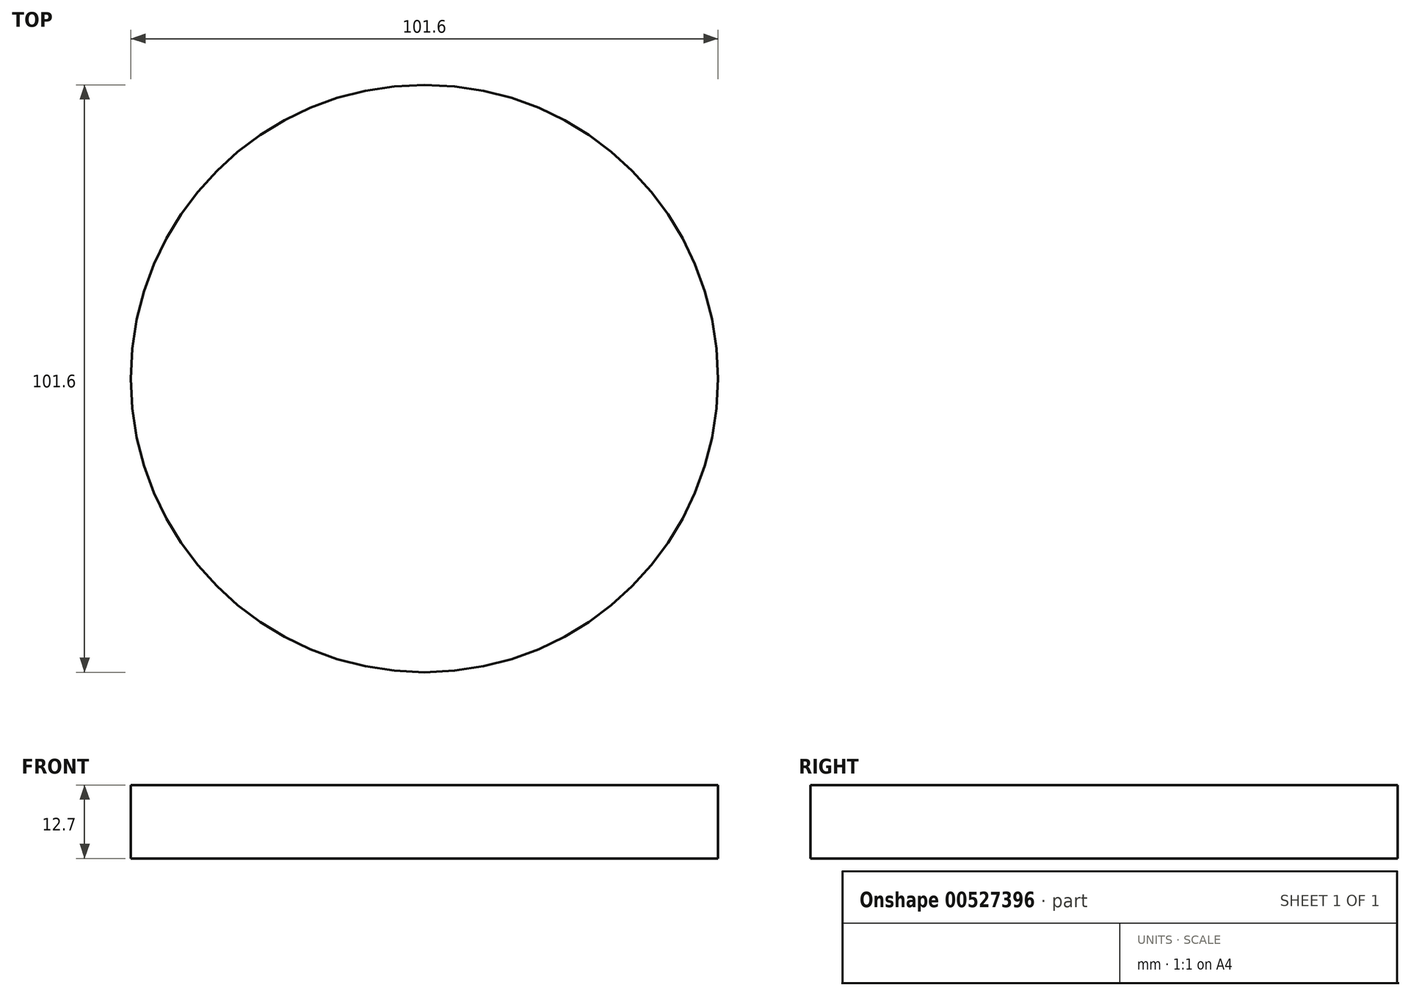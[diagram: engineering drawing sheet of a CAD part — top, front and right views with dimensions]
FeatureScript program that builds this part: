
annotation { "Feature Type Name" : "Feature", "Feature Type Description" : "" }
export const myFeature = defineFeature(function(context is Context, id is Id, definition is map)
    precondition{}
    {
        {
            var Q0;
            Q0=qCreatedBy(makeId("Top.planeOp"),FACE);
            var sketch = newSketch(context, id + "F0", { "sketchPlane" : qUnion([Q0])});
            skCircle(sketch, "E0", {"center": v(0, 0) * mm, "radius": 50.8 * mm});
            skSolve(sketch);
        }
        {
            var Q0;
            Q0 = qSketchRegion(id + "F0", true);
            extrude(context, id + "F1", {"entities" : qUnion([Q0]), "depth" : 12.7 * mm, "offsetDistance" : 25.4 * mm});
        }
    });
